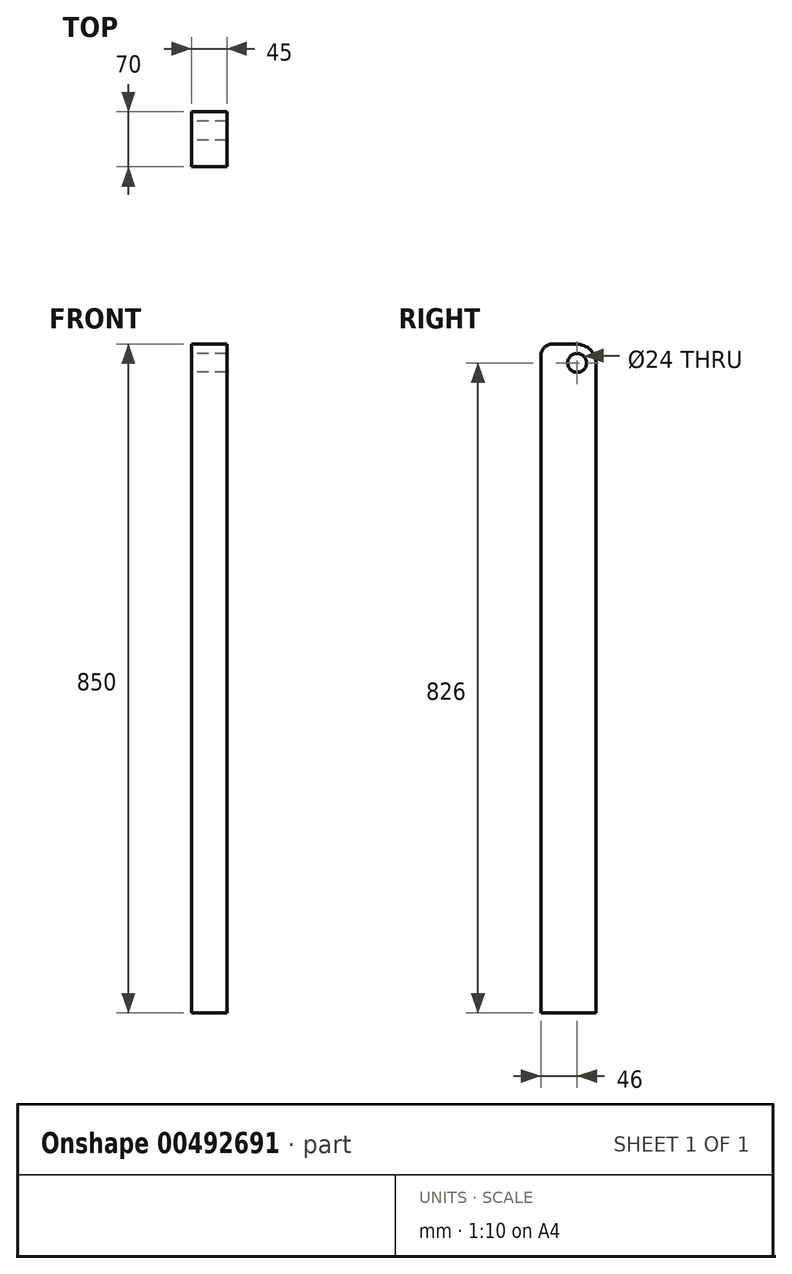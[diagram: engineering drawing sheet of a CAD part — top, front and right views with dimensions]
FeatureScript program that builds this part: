
annotation { "Feature Type Name" : "Feature", "Feature Type Description" : "" }
export const myFeature = defineFeature(function(context is Context, id is Id, definition is map)
    precondition{}
    {
        {
            var Q0;
            Q0=qCreatedBy(makeId("Front.planeOp"),FACE);
            var sketch = newSketch(context, id + "F0", { "sketchPlane" : qUnion([Q0])});
            skLineSegment(sketch, "E0.bottom", {"start": v(0, 0) * mm, "end": v(45, 0) * mm});
            skLineSegment(sketch, "E0.top", {"start": v(0, -850) * mm, "end": v(45, -850) * mm});
            skLineSegment(sketch, "E0.left", {"start": v(0, 0) * mm, "end": v(0, -850) * mm});
            skLineSegment(sketch, "E0.right", {"start": v(45, 0) * mm, "end": v(45, -850) * mm});
            skSolve(sketch);
        }
        {
            var Q0;
            Q0 = qSketchRegion(id + "F0", true);
            extrude(context, id + "F1", {"entities" : qUnion([Q0]), "depth" : 70 * mm});
        }
        {
            var Q0;
            Q0=makeQuery(id+"F1.opExtrude","SWEPT_FACE",FACE,{"disambiguationData":[OSD([sQuery(id+"F0.wireOp",EDGE,"E0.left")])]});
            var sketch = newSketch(context, id + "F2", { "sketchPlane" : qUnion([Q0])});
            skCircle(sketch, "E1", {"center": v(24, -24) * mm, "radius": 12 * mm});
            skSolve(sketch);
        }
        {
            var Q0;
            Q0 = qSketchRegion(id + "F2", true);
            extrude(context, id + "F3", {"entities" : qUnion([Q0]), "operationType" : NewBodyOperationType.REMOVE, "endBound" : BoundingType.THROUGH_ALL, "oppositeDirection" : true, "depth" : 25 * mm});
        }
        {
            var Q0;
            Q0=makeQuery(id+"F1.opExtrude","CAP_EDGE",EDGE,{"disambiguationData":[OSD([sQuery(id+"F0.wireOp",EDGE,"E0.bottom")])],"isStart":true});
            fillet(context, id + "F4", {"entities" : qUnion([Q0]), "radius" : 25 * mm, "tangentPropagation" : true, "allowEdgeOverflow" : false});
        }
        {
            var Q0;
            Q0=makeQuery(id+"F1.opExtrude","CAP_EDGE",EDGE,{"disambiguationData":[OSD([sQuery(id+"F0.wireOp",EDGE,"E0.bottom")])],"isStart":false});
            fillet(context, id + "F5", {"entities" : qUnion([Q0]), "radius" : 15 * mm, "tangentPropagation" : true, "allowEdgeOverflow" : false});
        }
    });
